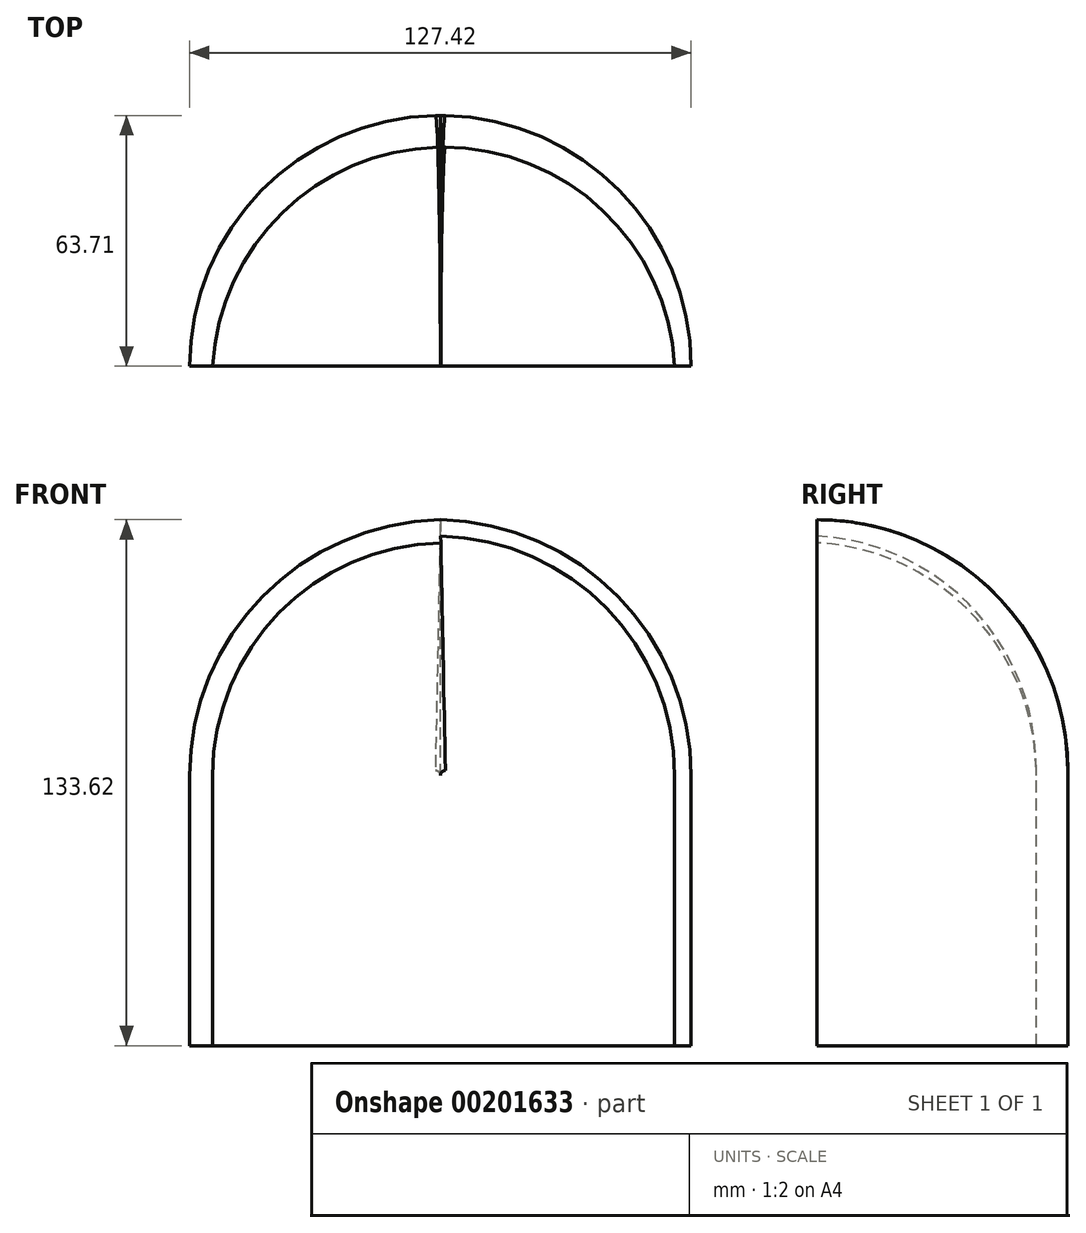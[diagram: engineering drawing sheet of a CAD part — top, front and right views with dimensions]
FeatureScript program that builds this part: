
annotation { "Feature Type Name" : "Feature", "Feature Type Description" : "" }
export const myFeature = defineFeature(function(context is Context, id is Id, definition is map)
    precondition{}
    {
        {
            var Q0;
            Q0=qCreatedBy(makeId("Top.planeOp"),FACE);
            var sketch = newSketch(context, id + "F0", { "sketchPlane" : qUnion([Q0])});
            skArc(sketch, "E0", {"start": v(23.2, -59.33) * mm, "mid": v(0.99, 63.7) * mm, "end": v(-25.04, -58.58) * mm});
            skPoint(sketch, "E1", {"position": v(-25.04, -58.58) * mm});
            skPoint(sketch, "E2", {"position": v(23.2, -59.33) * mm});
            skLineSegment(sketch, "E3", {"start": v(0, 0) * mm, "end": v(0, 63.7) * mm});
            skPoint(sketch, "E4", {"position": v(0, 63.7) * mm});
            skLineSegment(sketch, "E5", {"start": v(0, 0) * mm, "end": v(-63.7, 0) * mm});
            skLineSegment(sketch, "E6", {"start": v(0, 0) * mm, "end": v(63.7, 0) * mm});
            skPoint(sketch, "E7", {"position": v(-63.7, 0) * mm});
            skPoint(sketch, "E8", {"position": v(63.7, 0) * mm});
            skArc(sketch, "E9", {"start": v(59.54, 0) * mm, "mid": v(0.85, 55.67) * mm, "end": v(-57.85, 0) * mm});
            skSolve(sketch);
        }
        {
            var Q0;
            Q0=qCreatedBy(makeId("Right.planeOp"),FACE);
            var sketch = newSketch(context, id + "F1", { "sketchPlane" : qUnion([Q0])});
            skLineSegment(sketch, "E10.0", {"start": v(0, 0) * mm, "end": v(63.7, 0) * mm});
            skLineSegment(sketch, "E11", {"start": v(63.7, 0) * mm, "end": v(63.7, 68.63) * mm});
            skArc(sketch, "E12", {"start": v(63.7, 68.63) * mm, "mid": v(4.36, 133.39) * mm, "end": v(-65.32, 79.9) * mm});
            skPoint(sketch, "E13", {"position": v(0, 133.62) * mm});
            skLineSegment(sketch, "E14", {"start": v(0, 133.62) * mm, "end": v(-1.3, 68.63) * mm});
            skSolve(sketch);
        }
        {
            var Q0;
            Q0=qCreatedBy(makeId("Front.planeOp"),FACE);
            var sketch = newSketch(context, id + "F2", { "sketchPlane" : qUnion([Q0])});
            skLineSegment(sketch, "E15.0", {"start": v(0, 133.62) * mm, "end": v(0, 68.63) * mm});
            skLineSegment(sketch, "E16.0", {"start": v(0, 0) * mm, "end": v(-63.7, 0) * mm});
            skLineSegment(sketch, "E17", {"start": v(-63.7, 0) * mm, "end": v(-63.7, 68.63) * mm});
            skArc(sketch, "E18", {"start": v(0, 133.62) * mm, "mid": v(-45.12, 114.13) * mm, "end": v(-63.7, 68.63) * mm});
            skSolve(sketch);
        }
        {
            var Q0;
            Q0=qCreatedBy(makeId("Front.planeOp"),FACE);
            var sketch = newSketch(context, id + "F3", { "sketchPlane" : qUnion([Q0])});
            skLineSegment(sketch, "E19.0", {"start": v(0, 0) * mm, "end": v(63.7, 0) * mm});
            skLineSegment(sketch, "E20.0", {"start": v(0, 133.62) * mm, "end": v(0, 68.63) * mm});
            skLineSegment(sketch, "E21", {"start": v(63.7, 0) * mm, "end": v(63.7, 68.63) * mm});
            skArc(sketch, "E22", {"start": v(63.7, 68.63) * mm, "mid": v(45.12, 114.13) * mm, "end": v(0, 133.62) * mm});
            skSolve(sketch);
        }
        {
            var Q0;
            {var subQ0=sQuery(id+"F0.wireOp",EDGE,"E3");var subQ1=sQuery(id+"F0.wireOp",EDGE,"E0");var subQ2=makeQuery(id+"F0.imprint","INTERSECT",VERTEX,{"derivedFrom":[subQ1,subQ0]});Q0=makeQuery(id+"F0.imprint","IMPRINT",FACE,{"disambiguationData":[TD([[makeQuery(id+"F0.imprint","IMPRINT",EDGE,{"disambiguationData":[TD([[subQ2,1.0]])],"derivedFrom":subQ1}),1.0]])]});}
            var Q1;
            Q1=sQuery(id+"F3.wireOp",EDGE,"E21");
            var Q2;
            Q2=sQuery(id+"F3.wireOp",EDGE,"E22");
            sweep(context, id + "F4", {"profiles" : qUnion([Q0]), "path" : qUnion([Q1, Q2])});
        }
        {
            var Q0;
            {var subQ0=sQuery(id+"F0.wireOp",EDGE,"E3");var subQ1=sQuery(id+"F0.wireOp",EDGE,"E0");var subQ2=makeQuery(id+"F0.imprint","INTERSECT",VERTEX,{"derivedFrom":[subQ1,subQ0]});Q0=makeQuery(id+"F0.imprint","IMPRINT",FACE,{"disambiguationData":[TD([[makeQuery(id+"F0.imprint","IMPRINT",EDGE,{"disambiguationData":[TD([[subQ2,-1.0]])],"derivedFrom":subQ1}),1.0]])]});}
            var Q1;
            Q1=sQuery(id+"F2.wireOp",EDGE,"E18");
            var Q2;
            Q2=sQuery(id+"F2.wireOp",EDGE,"E17");
            sweep(context, id + "F5", {"operationType" : NewBodyOperationType.ADD, "profiles" : qUnion([Q0]), "path" : qUnion([Q1, Q2])});
        }
        {
            var Q0;
            Q0=qCreatedBy(makeId("Front.planeOp"),FACE);
            cPlane(context, id + "F6", {"entities" : qUnion([Q0]), "cplaneType" : CPlaneType.OFFSET, "offset" : 65.4 * mm, "width" : 152.4 * mm, "height" : 152.4 * mm});
        }
    });
